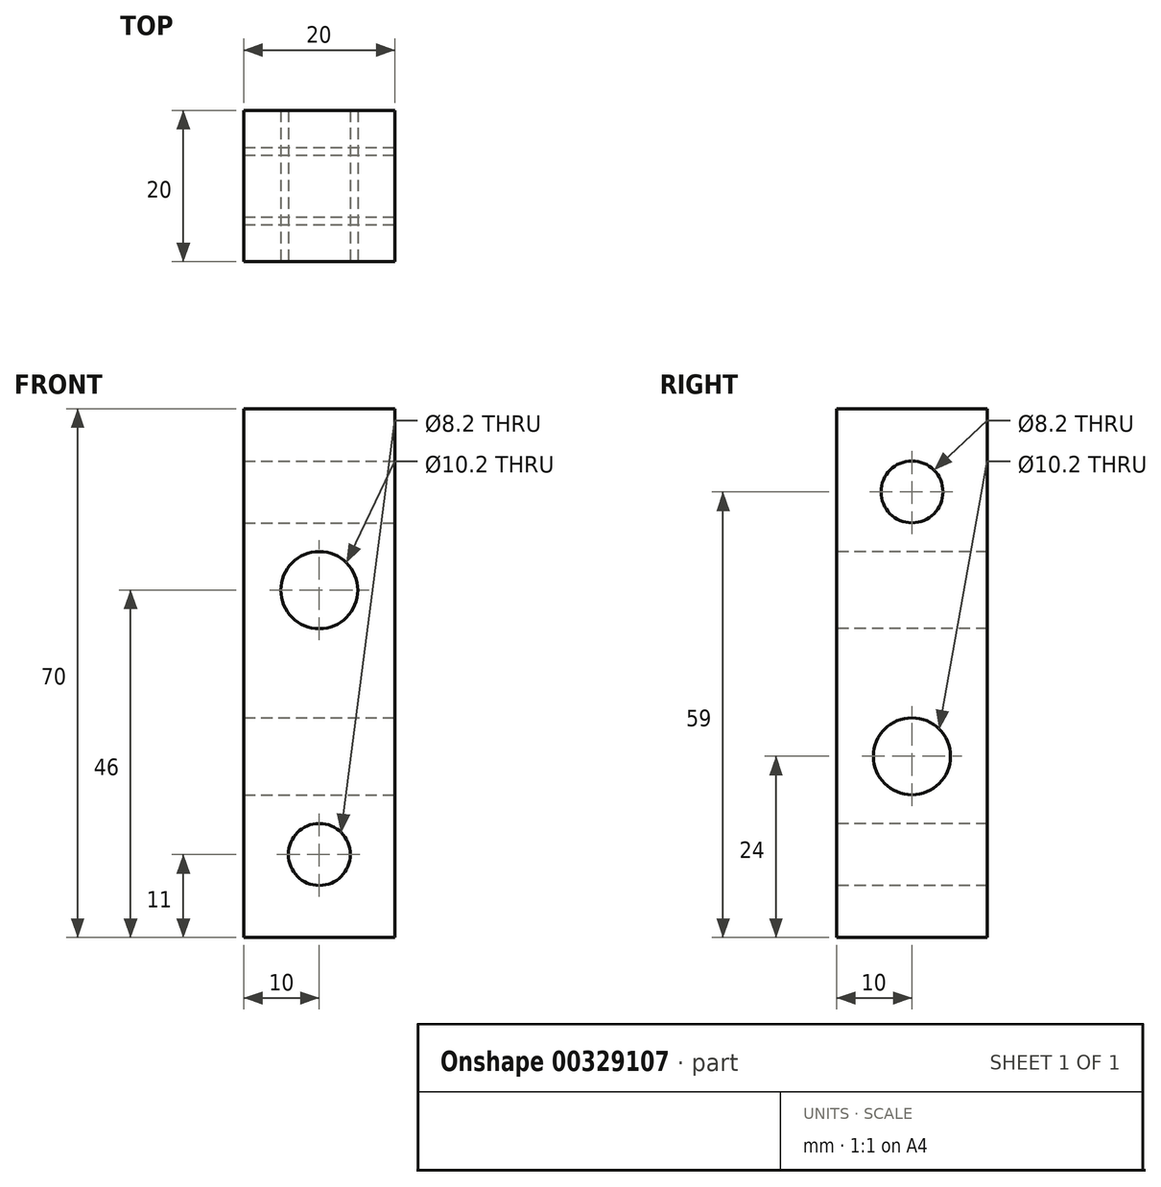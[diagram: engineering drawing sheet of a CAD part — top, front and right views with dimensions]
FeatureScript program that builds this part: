
annotation { "Feature Type Name" : "Feature", "Feature Type Description" : "" }
export const myFeature = defineFeature(function(context is Context, id is Id, definition is map)
    precondition{}
    {
        {
            var Q0;
            Q0=qCreatedBy(makeId("Top.planeOp"),FACE);
            var sketch = newSketch(context, id + "F0", { "sketchPlane" : qUnion([Q0])});
            skLineSegment(sketch, "E0.bottom", {"start": v(10, -10) * mm, "end": v(-10, -10) * mm});
            skLineSegment(sketch, "E0.top", {"start": v(10, 10) * mm, "end": v(-10, 10) * mm});
            skLineSegment(sketch, "E0.left", {"start": v(10, -10) * mm, "end": v(10, 10) * mm});
            skLineSegment(sketch, "E0.right", {"start": v(-10, -10) * mm, "end": v(-10, 10) * mm});
            skPoint(sketch, "E0.middle", {"position": v(0, 0) * mm});
            skSolve(sketch);
        }
        {
            var Q0;
            Q0 = qSketchRegion(id + "F0", true);
            extrude(context, id + "F1", {"entities" : qUnion([Q0]), "depth" : 70 * mm});
        }
        {
            var Q0;
            Q0=makeQuery(id+"F1.opExtrude","SWEPT_FACE",FACE,{"disambiguationData":[OSD([sQuery(id+"F0.wireOp",EDGE,"E0.bottom")])]});
            var sketch = newSketch(context, id + "F2", { "sketchPlane" : qUnion([Q0])});
            skLineSegment(sketch, "E1", {"start": v(0, 0) * mm, "end": v(0, 35) * mm, "construction": true});
            skPoint(sketch, "E1.endSnap0", {"position": v(0, 0) * mm});
            skLineSegment(sketch, "E2", {"start": v(0, 35) * mm, "end": v(0, 46) * mm, "construction": true});
            skCircle(sketch, "E3", {"center": v(0, 46) * mm, "radius": 5.1 * mm});
            skCircle(sketch, "E4", {"center": v(0, 11) * mm, "radius": 4.1 * mm});
            skSolve(sketch);
        }
        {
            var Q0;
            Q0 = qSketchRegion(id + "F2", true);
            extrude(context, id + "F3", {"entities" : qUnion([Q0]), "operationType" : NewBodyOperationType.REMOVE, "endBound" : BoundingType.THROUGH_ALL, "oppositeDirection" : true, "depth" : 25 * mm});
        }
        {
            var Q0;
            Q0=makeQuery(id+"F1.opExtrude","SWEPT_FACE",FACE,{"disambiguationData":[OSD([sQuery(id+"F0.wireOp",EDGE,"E0.left")])]});
            var sketch = newSketch(context, id + "F4", { "sketchPlane" : qUnion([Q0])});
            skLineSegment(sketch, "E5", {"start": v(0, 0) * mm, "end": v(0, 35) * mm, "construction": true});
            skLineSegment(sketch, "E6", {"start": v(0, 35) * mm, "end": v(0, 59) * mm, "construction": true});
            skCircle(sketch, "E7", {"center": v(0, 24) * mm, "radius": 5.1 * mm});
            skCircle(sketch, "E8", {"center": v(0, 59) * mm, "radius": 4.1 * mm});
            skSolve(sketch);
        }
        {
            var Q0;
            Q0 = qSketchRegion(id + "F4", true);
            extrude(context, id + "F5", {"entities" : qUnion([Q0]), "operationType" : NewBodyOperationType.REMOVE, "endBound" : BoundingType.THROUGH_ALL, "oppositeDirection" : true, "depth" : 25 * mm});
        }
    });
